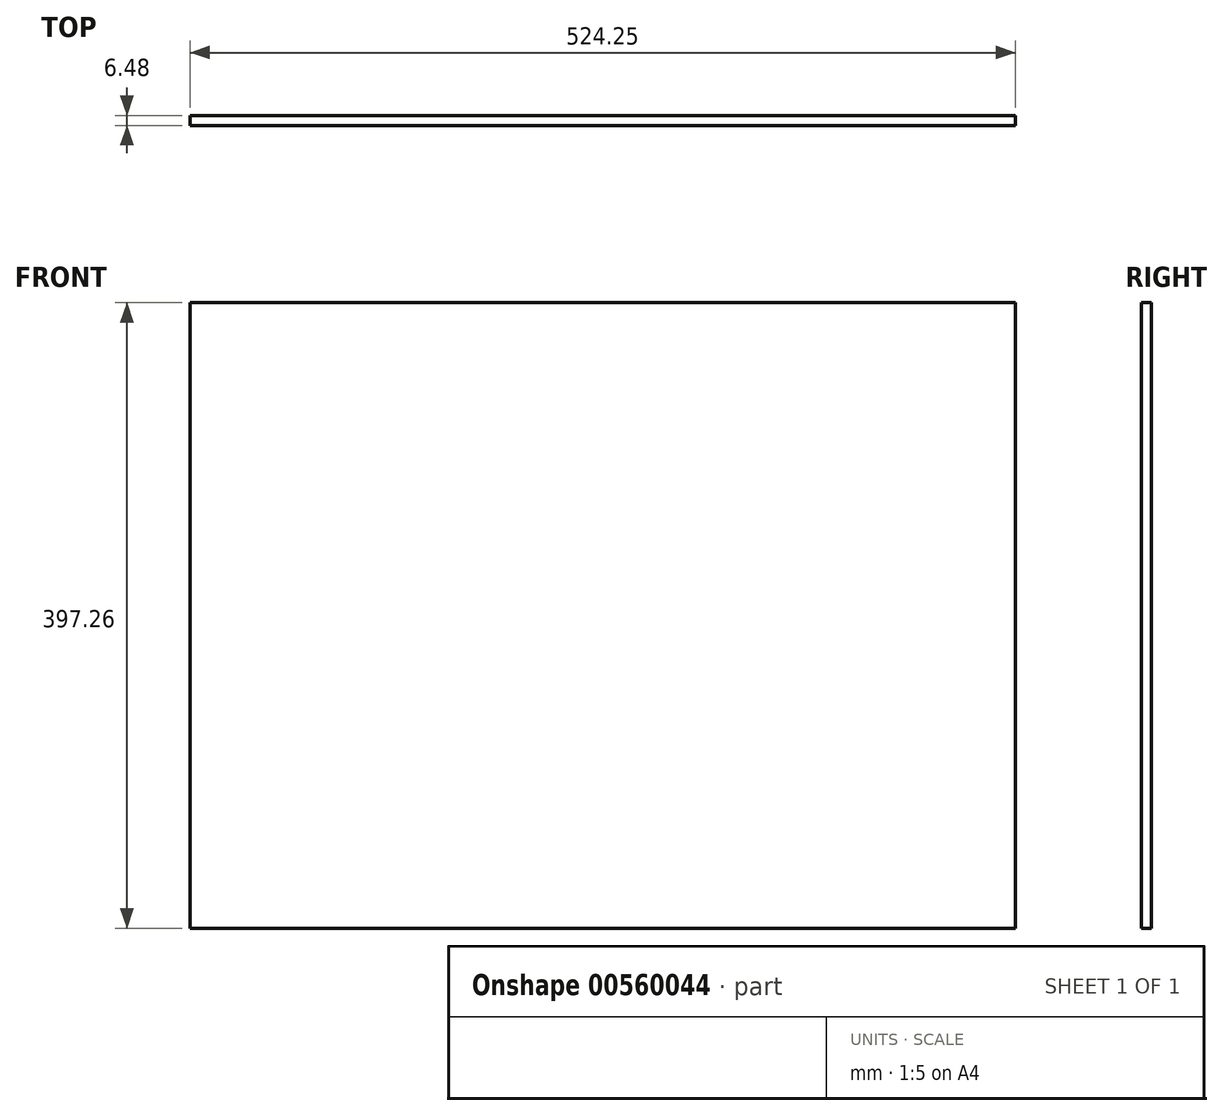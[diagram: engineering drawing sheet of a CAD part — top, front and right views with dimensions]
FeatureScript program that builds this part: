
annotation { "Feature Type Name" : "Feature", "Feature Type Description" : "" }
export const myFeature = defineFeature(function(context is Context, id is Id, definition is map)
    precondition{}
    {
        {
            var Q0;
            Q0=qCreatedBy(makeId("Front.planeOp"),FACE);
            var sketch = newSketch(context, id + "F0", { "sketchPlane" : qUnion([Q0])});
            skLineSegment(sketch, "E0.bottom", {"start": v(-261.72, 188.74) * mm, "end": v(262.53, 188.74) * mm});
            skLineSegment(sketch, "E0.top", {"start": v(-261.72, -208.52) * mm, "end": v(262.53, -208.52) * mm});
            skLineSegment(sketch, "E0.left", {"start": v(-261.72, 188.74) * mm, "end": v(-261.72, -208.52) * mm});
            skLineSegment(sketch, "E0.right", {"start": v(262.53, 188.74) * mm, "end": v(262.53, -208.52) * mm});
            skSolve(sketch);
        }
        {
            var Q0;
            Q0=makeQuery(id+"F0.imprint","IMPRINT",FACE,{"disambiguationData":[TD([[makeQuery(id+"F0.imprint","IMPRINT",EDGE,{"derivedFrom":sQuery(id+"F0.wireOp",EDGE,"E0.bottom")}),-1.0]])]});
            extrude(context, id + "F1", {"entities" : qUnion([Q0]), "depth" : 6.48 * mm, "offsetDistance" : 25.4 * mm});
        }
    });
